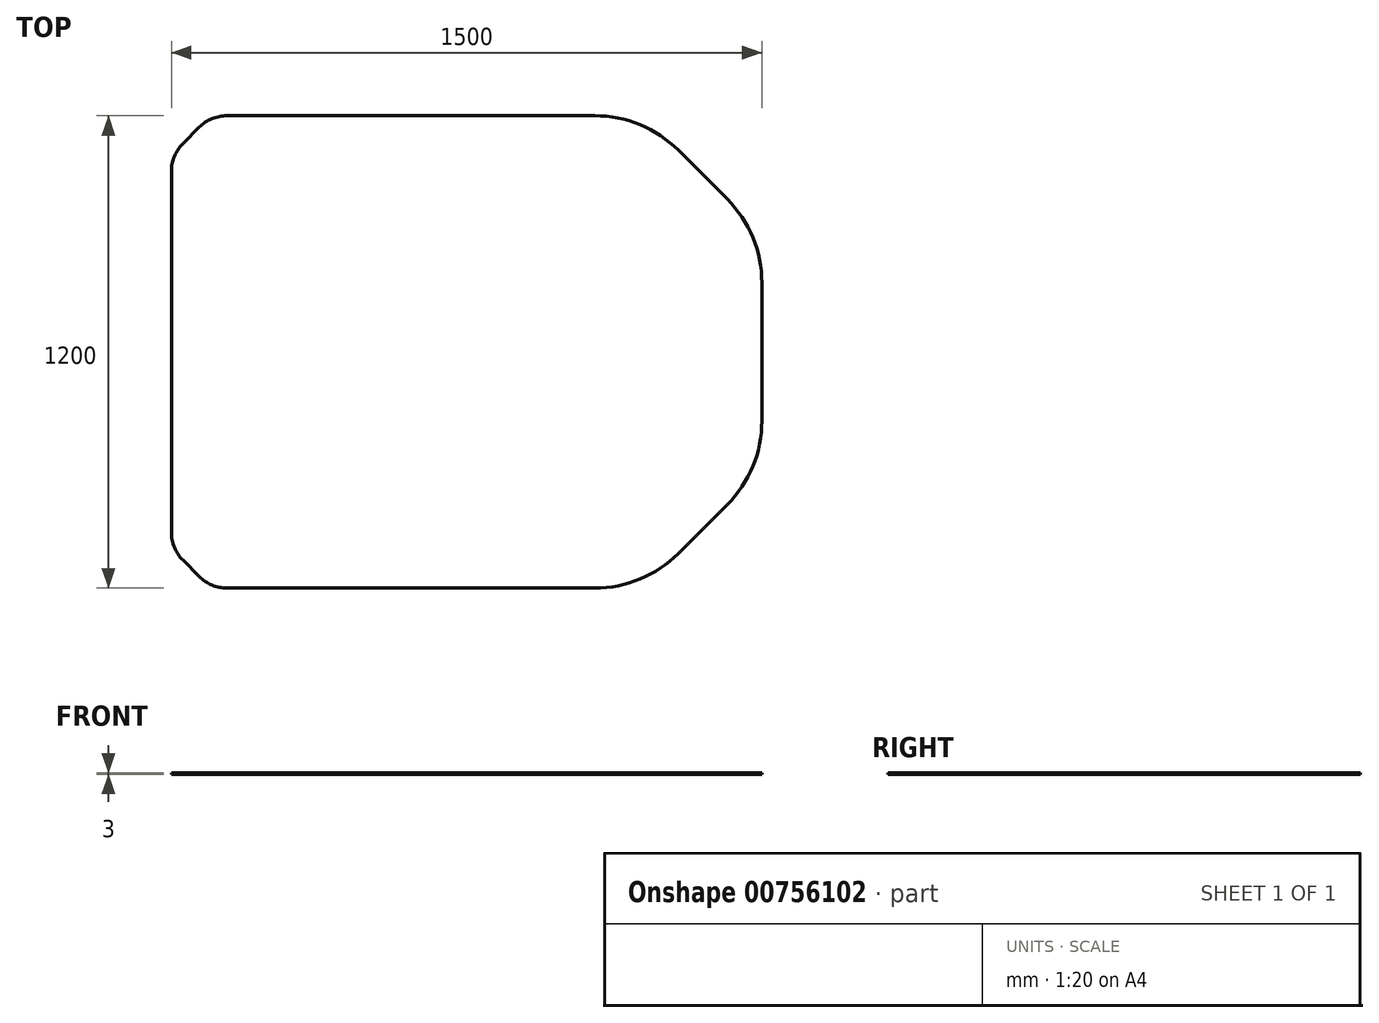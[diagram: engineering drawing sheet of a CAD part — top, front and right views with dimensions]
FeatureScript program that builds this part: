
annotation { "Feature Type Name" : "Feature", "Feature Type Description" : "" }
export const myFeature = defineFeature(function(context is Context, id is Id, definition is map)
    precondition{}
    {
        {
            var Q0;
            Q0=qCreatedBy(makeId("Top.planeOp"),FACE);
            var sketch = newSketch(context, id + "F0", { "sketchPlane" : qUnion([Q0])});
            skLineSegment(sketch, "E0.bottom", {"start": v(750, 600) * mm, "end": v(-750, 600) * mm});
            skLineSegment(sketch, "E0.top", {"start": v(750, -600) * mm, "end": v(-750, -600) * mm});
            skLineSegment(sketch, "E0.left", {"start": v(750, 600) * mm, "end": v(750, -600) * mm});
            skLineSegment(sketch, "E0.right", {"start": v(-750, 600) * mm, "end": v(-750, -600) * mm});
            skPoint(sketch, "E0.middle", {"position": v(0, 0) * mm});
            skSolve(sketch);
        }
        {
            var Q0;
            Q0 = qSketchRegion(id + "F0", true);
            extrude(context, id + "F1", {"entities" : qUnion([Q0]), "depth" : 3 * mm, "offsetDistance" : 25 * mm});
        }
        {
            var Q0;
            Q0=makeQuery(id+"F1.opExtrude","SWEPT_EDGE",EDGE,{"disambiguationData":[OSD([sQuery(id+"F0.wireOp",EDGE,"E0.top"),sQuery(id+"F0.wireOp",EDGE,"E0.left")])]});
            var Q1;
            Q1=makeQuery(id+"F1.opExtrude","SWEPT_EDGE",EDGE,{"disambiguationData":[OSD([sQuery(id+"F0.wireOp",EDGE,"E0.bottom"),sQuery(id+"F0.wireOp",EDGE,"E0.left")])]});
            chamfer(context, id + "F2", {"entities" : qUnion([Q0, Q1]), "width" : 300 * mm, "tangentPropagation" : true});
        }
        {
            var Q0;
            Q0=makeQuery(id+"F1.opExtrude","SWEPT_EDGE",EDGE,{"disambiguationData":[OSD([sQuery(id+"F0.wireOp",EDGE,"E0.top"),sQuery(id+"F0.wireOp",EDGE,"E0.right")])]});
            var Q1;
            Q1=makeQuery(id+"F1.opExtrude","SWEPT_EDGE",EDGE,{"disambiguationData":[OSD([sQuery(id+"F0.wireOp",EDGE,"E0.bottom"),sQuery(id+"F0.wireOp",EDGE,"E0.right")])]});
            chamfer(context, id + "F3", {"entities" : qUnion([Q0, Q1]), "width" : 100 * mm, "tangentPropagation" : true});
        }
        {
            var Q0;
            {var subQ0=sQuery(id+"F0.wireOp",EDGE,"E0.left");Q0=makeQuery(id+"F2.opChamfer","BLEND_EDGE",EDGE,{"blendedFrom":[makeQuery(id+"F1.opExtrude","SWEPT_EDGE",EDGE,{"disambiguationData":[OSD([sQuery(id+"F0.wireOp",EDGE,"E0.top"),subQ0])]}),makeQuery(id+"F1.opExtrude","SWEPT_FACE",FACE,{"disambiguationData":[OSD([subQ0])]})],"blendedInto":[makeQuery(id+"F1.opExtrude","SWEPT_FACE",FACE,{"disambiguationData":[OSD([subQ0])]})]});}
            var Q1;
            {var subQ0=sQuery(id+"F0.wireOp",EDGE,"E0.top");Q1=makeQuery(id+"F2.opChamfer","BLEND_EDGE",EDGE,{"blendedFrom":[makeQuery(id+"F1.opExtrude","SWEPT_EDGE",EDGE,{"disambiguationData":[OSD([subQ0,sQuery(id+"F0.wireOp",EDGE,"E0.left")])]}),makeQuery(id+"F1.opExtrude","SWEPT_FACE",FACE,{"disambiguationData":[OSD([subQ0])]})],"blendedInto":[makeQuery(id+"F1.opExtrude","SWEPT_FACE",FACE,{"disambiguationData":[OSD([subQ0])]})]});}
            var Q2;
            {var subQ0=sQuery(id+"F0.wireOp",EDGE,"E0.left");Q2=makeQuery(id+"F2.opChamfer","BLEND_EDGE",EDGE,{"blendedFrom":[makeQuery(id+"F1.opExtrude","SWEPT_EDGE",EDGE,{"disambiguationData":[OSD([sQuery(id+"F0.wireOp",EDGE,"E0.bottom"),subQ0])]}),makeQuery(id+"F1.opExtrude","SWEPT_FACE",FACE,{"disambiguationData":[OSD([subQ0])]})],"blendedInto":[makeQuery(id+"F1.opExtrude","SWEPT_FACE",FACE,{"disambiguationData":[OSD([subQ0])]})]});}
            var Q3;
            {var subQ0=sQuery(id+"F0.wireOp",EDGE,"E0.bottom");Q3=makeQuery(id+"F2.opChamfer","BLEND_EDGE",EDGE,{"blendedFrom":[makeQuery(id+"F1.opExtrude","SWEPT_EDGE",EDGE,{"disambiguationData":[OSD([subQ0,sQuery(id+"F0.wireOp",EDGE,"E0.left")])]}),makeQuery(id+"F1.opExtrude","SWEPT_FACE",FACE,{"disambiguationData":[OSD([subQ0])]})],"blendedInto":[makeQuery(id+"F1.opExtrude","SWEPT_FACE",FACE,{"disambiguationData":[OSD([subQ0])]})]});}
            fillet(context, id + "F4", {"entities" : qUnion([Q0, Q1, Q2, Q3]), "radius" : 300 * mm, "tangentPropagation" : true, "allowEdgeOverflow" : false});
        }
        {
            var Q0;
            {var subQ0=sQuery(id+"F0.wireOp",EDGE,"E0.right");Q0=makeQuery(id+"F3.opChamfer","BLEND_EDGE",EDGE,{"blendedFrom":[makeQuery(id+"F1.opExtrude","SWEPT_EDGE",EDGE,{"disambiguationData":[OSD([sQuery(id+"F0.wireOp",EDGE,"E0.top"),subQ0])]}),makeQuery(id+"F1.opExtrude","SWEPT_FACE",FACE,{"disambiguationData":[OSD([subQ0])]})],"blendedInto":[makeQuery(id+"F1.opExtrude","SWEPT_FACE",FACE,{"disambiguationData":[OSD([subQ0])]})]});}
            var Q1;
            {var subQ0=sQuery(id+"F0.wireOp",EDGE,"E0.top");Q1=makeQuery(id+"F3.opChamfer","BLEND_EDGE",EDGE,{"blendedFrom":[makeQuery(id+"F1.opExtrude","SWEPT_EDGE",EDGE,{"disambiguationData":[OSD([subQ0,sQuery(id+"F0.wireOp",EDGE,"E0.right")])]}),makeQuery(id+"F1.opExtrude","SWEPT_FACE",FACE,{"disambiguationData":[OSD([subQ0])]})],"blendedInto":[makeQuery(id+"F1.opExtrude","SWEPT_FACE",FACE,{"disambiguationData":[OSD([subQ0])]})]});}
            var Q2;
            {var subQ0=sQuery(id+"F0.wireOp",EDGE,"E0.bottom");Q2=makeQuery(id+"F3.opChamfer","BLEND_EDGE",EDGE,{"blendedFrom":[makeQuery(id+"F1.opExtrude","SWEPT_EDGE",EDGE,{"disambiguationData":[OSD([subQ0,sQuery(id+"F0.wireOp",EDGE,"E0.right")])]}),makeQuery(id+"F1.opExtrude","SWEPT_FACE",FACE,{"disambiguationData":[OSD([subQ0])]})],"blendedInto":[makeQuery(id+"F1.opExtrude","SWEPT_FACE",FACE,{"disambiguationData":[OSD([subQ0])]})]});}
            var Q3;
            {var subQ0=sQuery(id+"F0.wireOp",EDGE,"E0.right");Q3=makeQuery(id+"F3.opChamfer","BLEND_EDGE",EDGE,{"blendedFrom":[makeQuery(id+"F1.opExtrude","SWEPT_EDGE",EDGE,{"disambiguationData":[OSD([sQuery(id+"F0.wireOp",EDGE,"E0.bottom"),subQ0])]}),makeQuery(id+"F1.opExtrude","SWEPT_FACE",FACE,{"disambiguationData":[OSD([subQ0])]})],"blendedInto":[makeQuery(id+"F1.opExtrude","SWEPT_FACE",FACE,{"disambiguationData":[OSD([subQ0])]})]});}
            fillet(context, id + "F5", {"entities" : qUnion([Q0, Q1, Q2, Q3]), "radius" : 100 * mm, "tangentPropagation" : true, "allowEdgeOverflow" : false});
        }
    });
